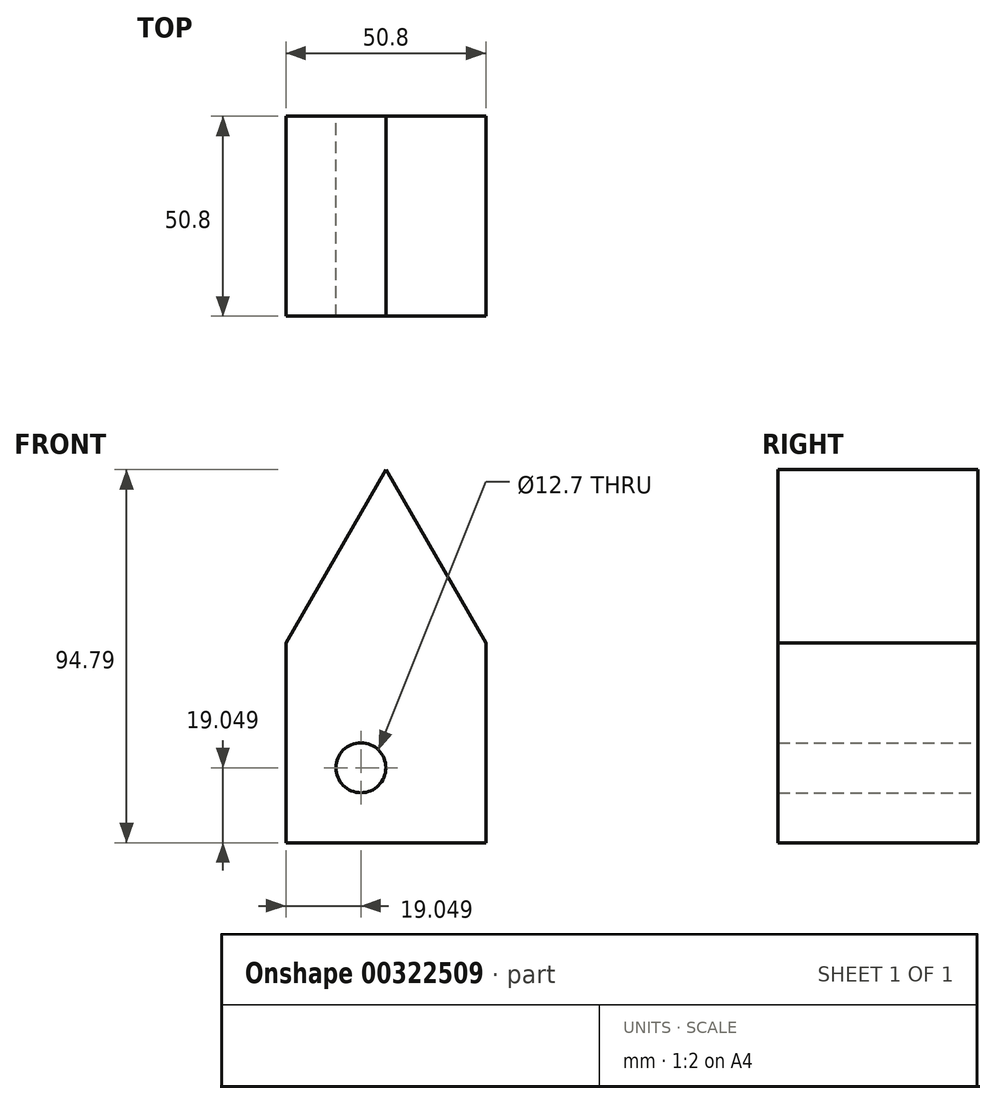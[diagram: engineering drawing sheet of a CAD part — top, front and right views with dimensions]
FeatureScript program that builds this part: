
annotation { "Feature Type Name" : "Feature", "Feature Type Description" : "" }
export const myFeature = defineFeature(function(context is Context, id is Id, definition is map)
    precondition{}
    {
        {
            var Q0;
            Q0=qCreatedBy(makeId("Front.planeOp"),FACE);
            var sketch = newSketch(context, id + "F0", { "sketchPlane" : qUnion([Q0])});
            skLineSegment(sketch, "E0.top", {"start": v(-38.41, -16.97) * mm, "end": v(12.39, -16.97) * mm});
            skLineSegment(sketch, "E0.left", {"start": v(-38.41, 33.83) * mm, "end": v(-38.41, -16.97) * mm});
            skLineSegment(sketch, "E0.right", {"start": v(12.39, 33.83) * mm, "end": v(12.39, -16.97) * mm});
            skLineSegment(sketch, "E1", {"start": v(-38.41, 33.83) * mm, "end": v(-13.01, 77.82) * mm});
            skLineSegment(sketch, "E2", {"start": v(12.39, 33.83) * mm, "end": v(-13.01, 77.82) * mm});
            skCircle(sketch, "E3", {"center": v(-19.36, 2.08) * mm, "radius": 6.35 * mm});
            skLineSegment(sketch, "E4", {"start": v(-38.41, -16.97) * mm, "end": v(-25.71, -16.97) * mm, "construction": true});
            skLineSegment(sketch, "E5.bottom", {"start": v(-38.41, -16.97) * mm, "end": v(-19.36, -16.97) * mm});
            skLineSegment(sketch, "E5.left", {"start": v(-38.41, -16.97) * mm, "end": v(-38.41, 2.08) * mm});
            skLineSegment(sketch, "E5.right", {"start": v(-19.36, -16.97) * mm, "end": v(-19.36, 2.08) * mm});
            skSolve(sketch);
        }
        {
            var Q0;
            Q0 = qSketchRegion(id + "F0", true);
            extrude(context, id + "F1", {"entities" : qUnion([Q0]), "depth" : 50.8 * mm});
        }
    });
